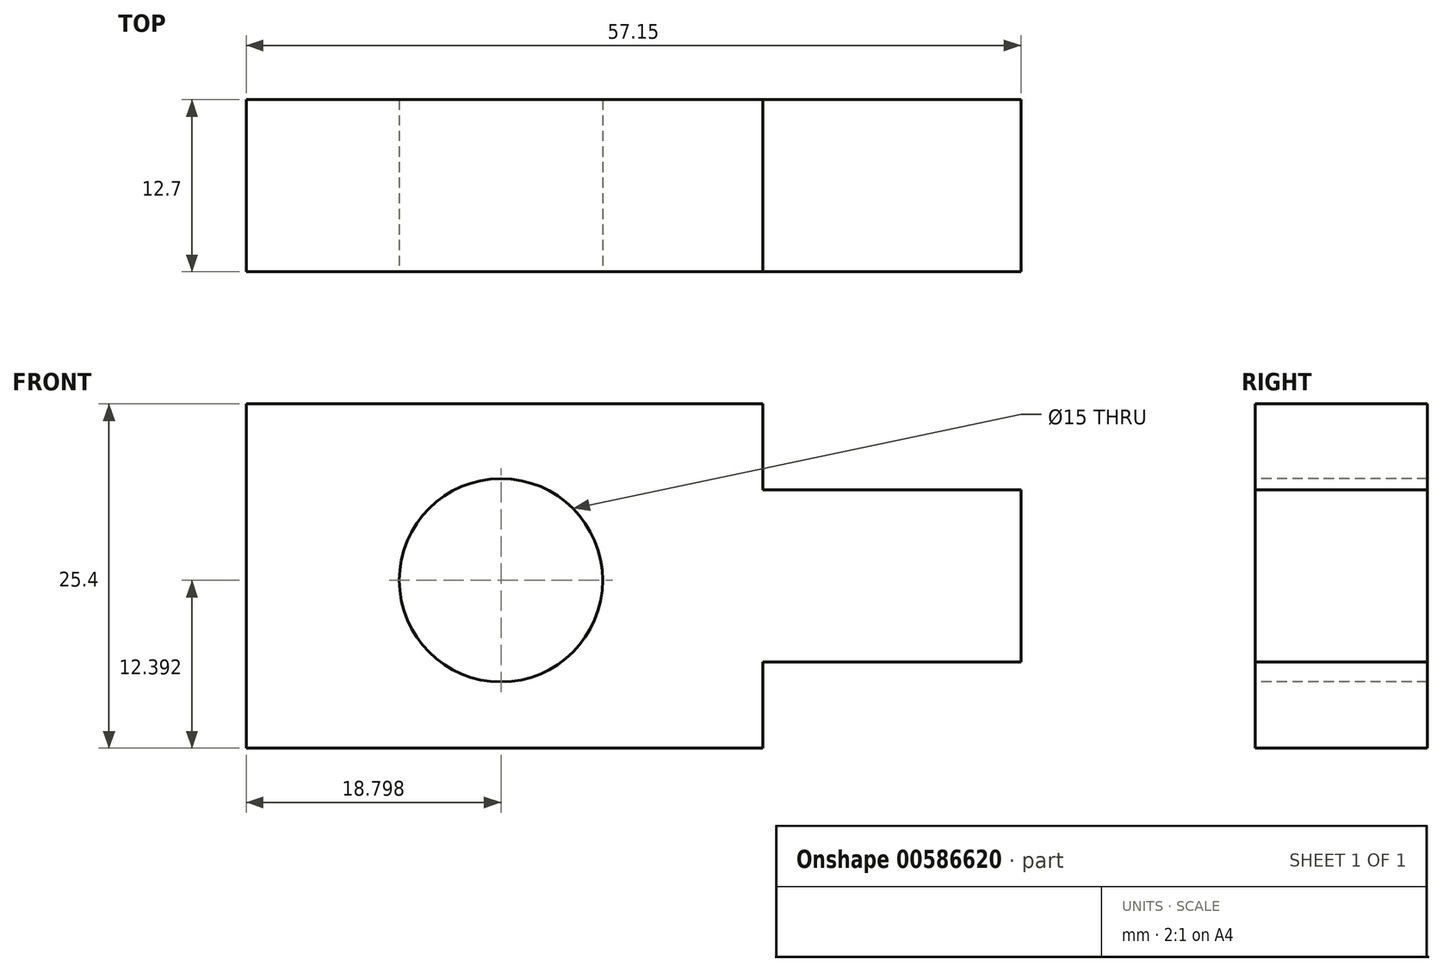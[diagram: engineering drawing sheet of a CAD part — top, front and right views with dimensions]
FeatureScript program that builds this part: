
annotation { "Feature Type Name" : "Feature", "Feature Type Description" : "" }
export const myFeature = defineFeature(function(context is Context, id is Id, definition is map)
    precondition{}
    {
        {
            var Q0;
            Q0=qCreatedBy(makeId("Front.planeOp"),FACE);
            var sketch = newSketch(context, id + "F0", { "sketchPlane" : qUnion([Q0])});
            skLineSegment(sketch, "E0", {"start": v(0, 0) * mm, "end": v(0, 25.4) * mm});
            skLineSegment(sketch, "E1", {"start": v(0, 25.4) * mm, "end": v(38.1, 25.4) * mm});
            skLineSegment(sketch, "E2", {"start": v(38.1, 25.4) * mm, "end": v(38.1, 19.05) * mm});
            skLineSegment(sketch, "E3", {"start": v(38.1, 19.05) * mm, "end": v(57.15, 19.05) * mm});
            skLineSegment(sketch, "E4", {"start": v(57.15, 19.05) * mm, "end": v(57.15, 6.35) * mm});
            skLineSegment(sketch, "E5", {"start": v(57.15, 6.35) * mm, "end": v(38.1, 6.35) * mm});
            skLineSegment(sketch, "E6", {"start": v(38.1, 6.35) * mm, "end": v(38.1, 0) * mm});
            skLineSegment(sketch, "E7", {"start": v(38.1, 0) * mm, "end": v(0, 0) * mm});
            skSolve(sketch);
        }
        {
            var Q0;
            Q0 = qSketchRegion(id + "F0", true);
            extrude(context, id + "F1", {"entities" : qUnion([Q0]), "depth" : 12.7 * mm, "offsetDistance" : 25.4 * mm});
        }
        {
            var Q0;
            Q0=makeQuery(id+"F1.opExtrude","CAP_FACE",FACE,{"disambiguationData":[OSD([sQuery(id+"F0.wireOp",EDGE,"E0"),sQuery(id+"F0.wireOp",EDGE,"E1"),sQuery(id+"F0.wireOp",EDGE,"E2"),sQuery(id+"F0.wireOp",EDGE,"E3"),sQuery(id+"F0.wireOp",EDGE,"E4"),sQuery(id+"F0.wireOp",EDGE,"E5"),sQuery(id+"F0.wireOp",EDGE,"E6"),sQuery(id+"F0.wireOp",EDGE,"E7")])],"isStart":false});
            var sketch = newSketch(context, id + "F2", { "sketchPlane" : qUnion([Q0])});
            skCircle(sketch, "E8", {"center": v(18.8, 12.4) * mm, "radius": 7.5 * mm});
            skSolve(sketch);
        }
        {
            var Q0;
            Q0=makeQuery(id+"F2.imprint","IMPRINT",FACE,{"disambiguationData":[TD([[makeQuery(id+"F2.imprint","IMPRINT",EDGE,{"derivedFrom":sQuery(id+"F2.wireOp",EDGE,"E8")}),1.0]])]});
            extrude(context, id + "F3", {"entities" : qUnion([Q0]), "operationType" : NewBodyOperationType.REMOVE, "oppositeDirection" : true, "depth" : 25.4 * mm, "offsetDistance" : 25.4 * mm});
        }
    });
